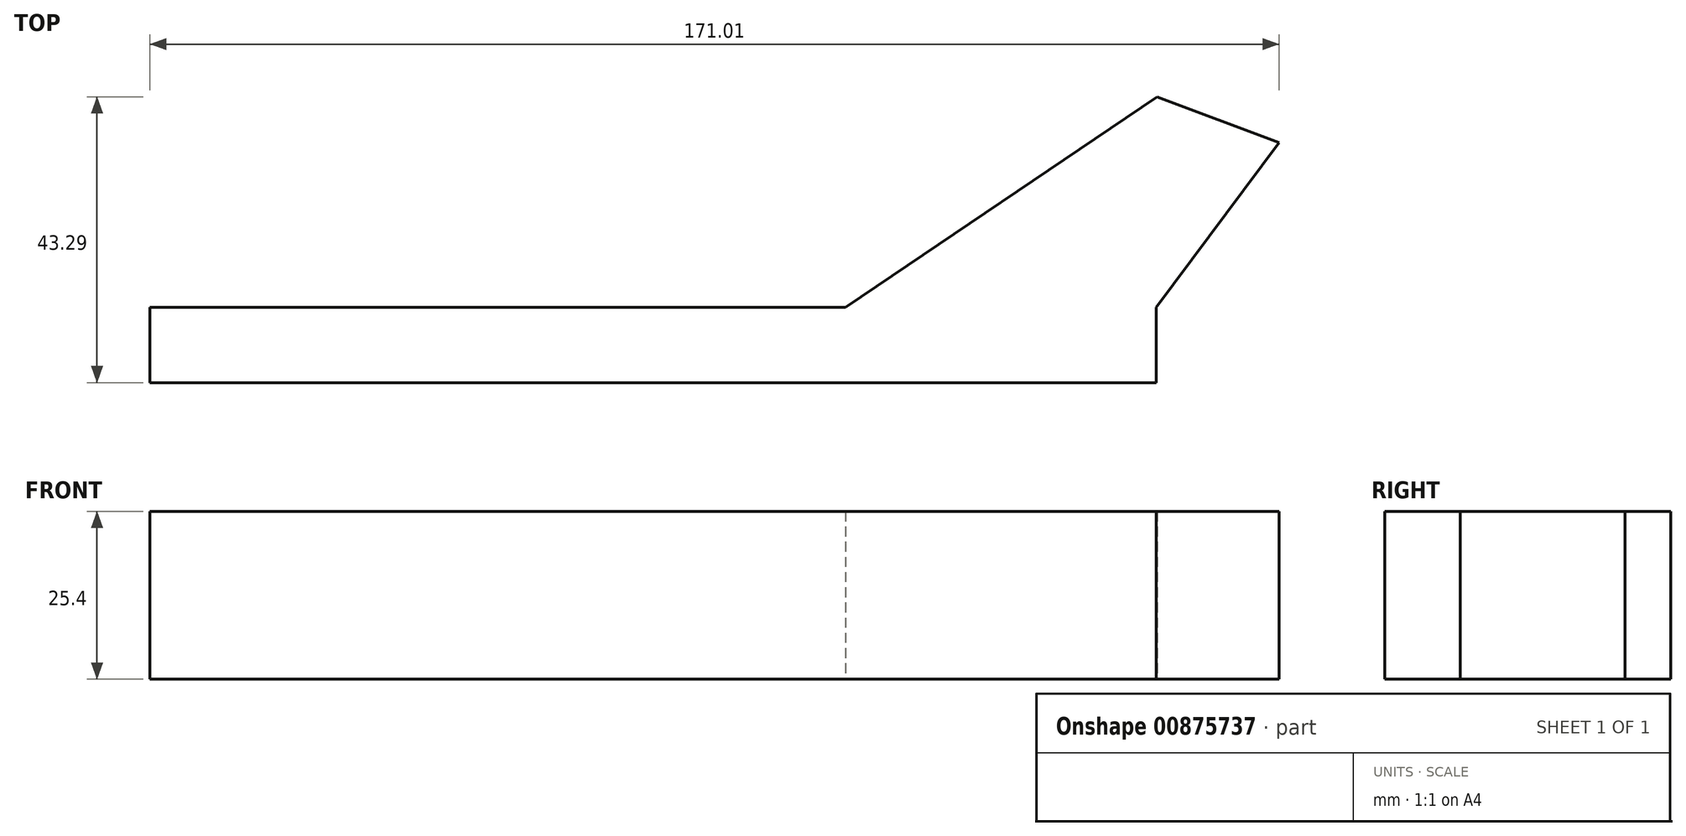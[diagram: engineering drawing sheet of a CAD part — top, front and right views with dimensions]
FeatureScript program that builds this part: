
annotation { "Feature Type Name" : "Feature", "Feature Type Description" : "" }
export const myFeature = defineFeature(function(context is Context, id is Id, definition is map)
    precondition{}
    {
        {
            var Q0;
            Q0=qCreatedBy(makeId("Top.planeOp"),FACE);
            var sketch = newSketch(context, id + "F0", { "sketchPlane" : qUnion([Q0])});
            skLineSegment(sketch, "E0.bottom", {"start": v(15, 0) * mm, "end": v(-64.76, 0) * mm});
            skLineSegment(sketch, "E0.top", {"start": v(15, 11.42) * mm, "end": v(-64.76, 11.42) * mm});
            skLineSegment(sketch, "E0.left", {"start": v(15, 0) * mm, "end": v(15, 11.42) * mm});
            skLineSegment(sketch, "E0.right", {"start": v(-64.76, 0) * mm, "end": v(-64.76, 11.42) * mm});
            skLineSegment(sketch, "E1", {"start": v(-32.04, 11.42) * mm, "end": v(15.17, 43.29) * mm});
            skLineSegment(sketch, "E2", {"start": v(15, 11.42) * mm, "end": v(33.6, 36.4) * mm});
            skLineSegment(sketch, "E3", {"start": v(33.6, 36.4) * mm, "end": v(15.17, 43.29) * mm});
            skSolve(sketch);
        }
        {
            var Q0;
            Q0 = qSketchRegion(id + "F0", true);
            extrude(context, id + "F1", {"entities" : qUnion([Q0]), "depth" : 25.4 * mm, "offsetDistance" : 25.4 * mm});
        }
        {
            var Q0;
            Q0=makeQuery(id+"F1.opExtrude","SWEPT_FACE",FACE,{"disambiguationData":[OSD([sQuery(id+"F0.wireOp",EDGE,"E0.left")])]});
            extrude(context, id + "F2", {"entities" : qUnion([Q0]), "operationType" : NewBodyOperationType.ADD, "depth" : -152.4 * mm, "offsetDistance" : 25.4 * mm});
        }
    });
